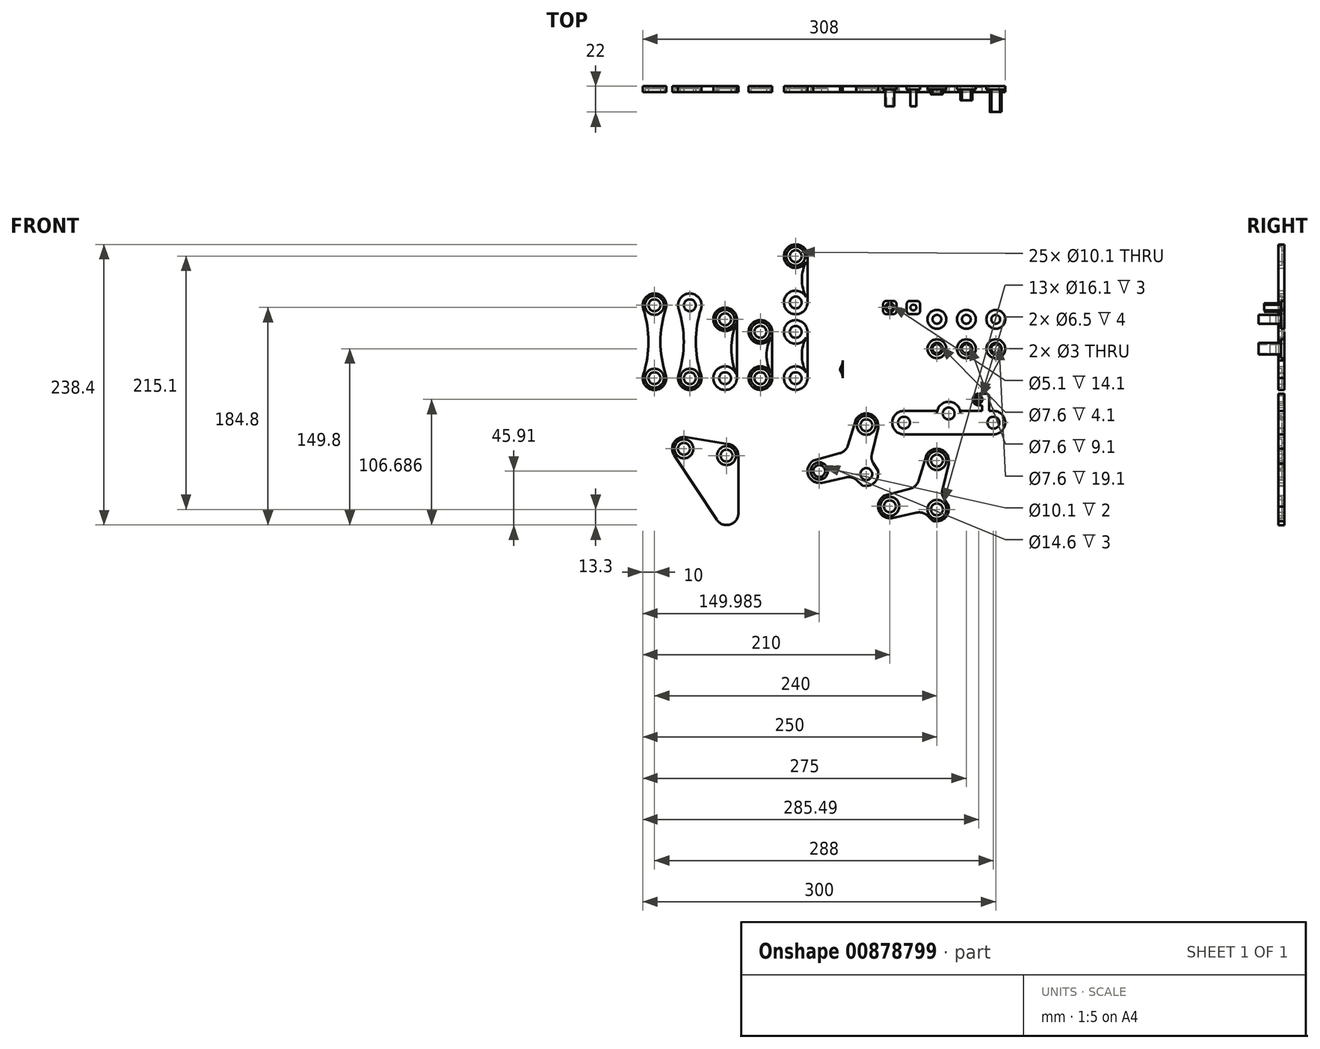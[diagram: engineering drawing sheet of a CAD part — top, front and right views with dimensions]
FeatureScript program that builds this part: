
annotation { "Feature Type Name" : "Feature", "Feature Type Description" : "" }
export const myFeature = defineFeature(function(context is Context, id is Id, definition is map)
    precondition{}
    {
        {
            assignVariable(context, id + "F0", {"name" : "thinkress", "anyValue" : 5});
        }
        {
            var Q0;
            Q0=qCreatedBy(makeId("Front.planeOp"),FACE);
            var sketch = newSketch(context, id + "F1", { "sketchPlane" : qUnion([Q0])});
            skArc(sketch, "E0", {"start": v(-10, 15) * mm, "mid": v(-20, 25) * mm, "end": v(-30, 15) * mm});
            skLineSegment(sketch, "E1", {"start": v(-30, 15) * mm, "end": v(-30, 0) * mm});
            skLineSegment(sketch, "E2", {"start": v(-10, 15) * mm, "end": v(-10, 0) * mm});
            skCircle(sketch, "E3", {"center": v(-20, 15) * mm, "radius": 5.05 * mm});
            skCircle(sketch, "E4", {"center": v(-20, 0) * mm, "radius": 5.05 * mm});
            skArc(sketch, "E5", {"start": v(-60, 0) * mm, "mid": v(-50, -10) * mm, "end": v(-40, 0) * mm});
            skArc(sketch, "E6", {"start": v(-40, 39.3) * mm, "mid": v(-50, 49.3) * mm, "end": v(-60, 39.3) * mm});
            skLineSegment(sketch, "E7", {"start": v(-60, 39.3) * mm, "end": v(-60, 0) * mm});
            skLineSegment(sketch, "E8", {"start": v(-40, 39.3) * mm, "end": v(-40, 0) * mm});
            skCircle(sketch, "E9", {"center": v(-50, 39.3) * mm, "radius": 5.05 * mm});
            skCircle(sketch, "E10", {"center": v(-50, 0) * mm, "radius": 5.05 * mm});
            skArc(sketch, "E11", {"start": v(-90, 0) * mm, "mid": v(-80, -10) * mm, "end": v(-70, 0) * mm});
            skArc(sketch, "E12", {"start": v(-70, 39.4) * mm, "mid": v(-80, 49.4) * mm, "end": v(-90, 39.4) * mm});
            skLineSegment(sketch, "E13", {"start": v(-90, 39.4) * mm, "end": v(-90, 0) * mm});
            skLineSegment(sketch, "E14", {"start": v(-70, 39.4) * mm, "end": v(-70, 0) * mm});
            skCircle(sketch, "E15", {"center": v(-80, 39.4) * mm, "radius": 5.05 * mm});
            skCircle(sketch, "E16", {"center": v(-80, 0) * mm, "radius": 5.05 * mm});
            skArc(sketch, "E17", {"start": v(-120, 0) * mm, "mid": v(-110, -10) * mm, "end": v(-100, 0) * mm});
            skArc(sketch, "E18", {"start": v(-100, 50) * mm, "mid": v(-110, 60) * mm, "end": v(-120, 50) * mm});
            skLineSegment(sketch, "E19", {"start": v(-120, 50) * mm, "end": v(-120, 0) * mm});
            skLineSegment(sketch, "E20", {"start": v(-100, 50) * mm, "end": v(-100, 0) * mm});
            skCircle(sketch, "E21", {"center": v(-110, 50) * mm, "radius": 5.05 * mm});
            skCircle(sketch, "E22", {"center": v(-110, 0) * mm, "radius": 5.05 * mm});
            skArc(sketch, "E23", {"start": v(-150, 0) * mm, "mid": v(-140, -10) * mm, "end": v(-130, 0) * mm});
            skArc(sketch, "E24", {"start": v(-130, 61.9) * mm, "mid": v(-140, 71.9) * mm, "end": v(-150, 61.9) * mm});
            skLineSegment(sketch, "E25", {"start": v(-150, 61.9) * mm, "end": v(-150, 0) * mm});
            skLineSegment(sketch, "E26", {"start": v(-130, 61.9) * mm, "end": v(-130, 0) * mm});
            skCircle(sketch, "E27", {"center": v(-140, 61.9) * mm, "radius": 5.05 * mm});
            skCircle(sketch, "E28", {"center": v(-140, 0) * mm, "radius": 5.05 * mm});
            skLineSegment(sketch, "E29", {"start": v(10, -81.5) * mm, "end": v(10, -40) * mm, "construction": true});
            skLineSegment(sketch, "E30", {"start": v(10, -40) * mm, "end": v(-30.01, -78.9) * mm, "construction": true});
            skLineSegment(sketch, "E31", {"start": v(-30.01, -78.9) * mm, "end": v(10, -81.5) * mm, "construction": true});
            skLineSegment(sketch, "E32", {"start": v(-145, -60) * mm, "end": v(-108.76, -65.8) * mm, "construction": true});
            skPoint(sketch, "E32.startSnap0", {"position": v(-80, -10) * mm});
            skLineSegment(sketch, "E33", {"start": v(-108.76, -65.8) * mm, "end": v(-108.76, -114.8) * mm, "construction": true});
            skLineSegment(sketch, "E34", {"start": v(-108.76, -114.8) * mm, "end": v(-145, -60) * mm, "construction": true});
            skArc(sketch, "E35", {"start": v(20, -40) * mm, "mid": v(13.9, -30.79) * mm, "end": v(3.03, -32.83) * mm});
            skArc(sketch, "E36", {"start": v(9.35, -91.48) * mm, "mid": v(16.84, -88.8) * mm, "end": v(20, -81.5) * mm});
            skArc(sketch, "E37", {"start": v(-36.98, -71.72) * mm, "mid": v(-39.4, -82.35) * mm, "end": v(-30.67, -88.87) * mm});
            skLineSegment(sketch, "E38.0", {"start": v(3.03, -32.83) * mm, "end": v(-36.98, -71.72) * mm});
            skLineSegment(sketch, "E39.0", {"start": v(20, -81.5) * mm, "end": v(20, -40) * mm});
            skLineSegment(sketch, "E40.0", {"start": v(-30.67, -88.87) * mm, "end": v(9.35, -91.48) * mm});
            skCircle(sketch, "E41", {"center": v(-30.01, -78.9) * mm, "radius": 5.05 * mm});
            skCircle(sketch, "E42", {"center": v(10, -40) * mm, "radius": 5.05 * mm});
            skCircle(sketch, "E43", {"center": v(10, -81.5) * mm, "radius": 5.05 * mm});
            skArc(sketch, "E44", {"start": v(-143.42, -50.13) * mm, "mid": v(-153.4, -54.58) * mm, "end": v(-153.34, -65.52) * mm});
            skArc(sketch, "E45", {"start": v(-117.1, -120.32) * mm, "mid": v(-105.88, -124.38) * mm, "end": v(-98.76, -114.8) * mm});
            skArc(sketch, "E46", {"start": v(-98.76, -65.8) * mm, "mid": v(-101.15, -59.31) * mm, "end": v(-107.18, -55.93) * mm});
            skLineSegment(sketch, "E47.0", {"start": v(-117.1, -120.32) * mm, "end": v(-153.34, -65.52) * mm});
            skLineSegment(sketch, "E48.0", {"start": v(-143.42, -50.13) * mm, "end": v(-107.18, -55.93) * mm});
            skLineSegment(sketch, "E49.0", {"start": v(-98.76, -65.8) * mm, "end": v(-98.76, -114.8) * mm});
            skCircle(sketch, "E50", {"center": v(-145, -60) * mm, "radius": 5.05 * mm});
            skCircle(sketch, "E51", {"center": v(-108.76, -65.8) * mm, "radius": 5.05 * mm});
            skLineSegment(sketch, "E52", {"start": v(42, -37.8) * mm, "end": v(80, -37.8) * mm, "construction": true});
            skLineSegment(sketch, "E53", {"start": v(80, -37.8) * mm, "end": v(118, -37.8) * mm, "construction": true});
            skLineSegment(sketch, "E54", {"start": v(80, -37.8) * mm, "end": v(80, -30) * mm, "construction": true});
            skArc(sketch, "E55", {"start": v(42, -27.8) * mm, "mid": v(32, -37.8) * mm, "end": v(42, -47.8) * mm});
            skArc(sketch, "E56", {"start": v(118, -47.8) * mm, "mid": v(128, -37.8) * mm, "end": v(118, -27.8) * mm});
            skArc(sketch, "E57", {"start": v(90, -30) * mm, "mid": v(80, -20) * mm, "end": v(70, -30) * mm});
            skLineSegment(sketch, "E58", {"start": v(42, -47.8) * mm, "end": v(118, -47.8) * mm});
            skLineSegment(sketch, "E59", {"start": v(42, -27.8) * mm, "end": v(70, -27.8) * mm});
            skLineSegment(sketch, "E60", {"start": v(70, -27.8) * mm, "end": v(70, -30) * mm});
            skLineSegment(sketch, "E61", {"start": v(118, -27.8) * mm, "end": v(114.5, -27.8) * mm});
            skLineSegment(sketch, "E62", {"start": v(90, -27.8) * mm, "end": v(90, -30) * mm});
            skCircle(sketch, "E63", {"center": v(80, -30) * mm, "radius": 5.05 * mm});
            skCircle(sketch, "E64", {"center": v(118, -37.8) * mm, "radius": 5.05 * mm});
            skCircle(sketch, "E65", {"center": v(42, -37.8) * mm, "radius": 5.05 * mm});
            skArc(sketch, "E66", {"start": v(-30, 0) * mm, "mid": v(-20, -10) * mm, "end": v(-10, 0) * mm});
            skArc(sketch, "E67", {"start": v(-180, 0) * mm, "mid": v(-170, -10) * mm, "end": v(-160, 0) * mm});
            skArc(sketch, "E68", {"start": v(-160, 61.9) * mm, "mid": v(-170, 71.9) * mm, "end": v(-180, 61.9) * mm});
            skLineSegment(sketch, "E69", {"start": v(-180, 61.9) * mm, "end": v(-180, 0) * mm});
            skLineSegment(sketch, "E70", {"start": v(-160, 61.9) * mm, "end": v(-160, 0) * mm});
            skCircle(sketch, "E71", {"center": v(-170, 61.9) * mm, "radius": 5.05 * mm});
            skCircle(sketch, "E72", {"center": v(-170, 0) * mm, "radius": 5.05 * mm});
            skLineSegment(sketch, "E73", {"start": v(70, -111.5) * mm, "end": v(70, -70) * mm, "construction": true});
            skLineSegment(sketch, "E74", {"start": v(70, -70) * mm, "end": v(29.99, -108.9) * mm, "construction": true});
            skLineSegment(sketch, "E75", {"start": v(29.99, -108.9) * mm, "end": v(70, -111.5) * mm, "construction": true});
            skArc(sketch, "E76", {"start": v(80, -70) * mm, "mid": v(73.9, -60.79) * mm, "end": v(63.03, -62.83) * mm});
            skArc(sketch, "E77", {"start": v(69.35, -121.48) * mm, "mid": v(76.84, -118.8) * mm, "end": v(80, -111.5) * mm});
            skArc(sketch, "E78", {"start": v(23.02, -101.72) * mm, "mid": v(20.6, -112.35) * mm, "end": v(29.33, -118.87) * mm});
            skLineSegment(sketch, "E79.0", {"start": v(63.03, -62.83) * mm, "end": v(23.02, -101.72) * mm});
            skLineSegment(sketch, "E80.0", {"start": v(80, -111.5) * mm, "end": v(80, -70) * mm});
            skLineSegment(sketch, "E81.0", {"start": v(29.33, -118.87) * mm, "end": v(69.35, -121.48) * mm});
            skCircle(sketch, "E82", {"center": v(29.99, -108.9) * mm, "radius": 5.05 * mm});
            skCircle(sketch, "E83", {"center": v(70, -70) * mm, "radius": 5.05 * mm});
            skCircle(sketch, "E84", {"center": v(70, -111.5) * mm, "radius": 5.05 * mm});
            skArc(sketch, "E85", {"start": v(-60, 64.3) * mm, "mid": v(-50, 54.3) * mm, "end": v(-40, 64.3) * mm});
            skArc(sketch, "E86", {"start": v(-40, 103.6) * mm, "mid": v(-50, 113.6) * mm, "end": v(-60, 103.6) * mm});
            skLineSegment(sketch, "E87", {"start": v(-60, 103.6) * mm, "end": v(-60, 64.3) * mm});
            skLineSegment(sketch, "E88", {"start": v(-40, 103.6) * mm, "end": v(-40, 64.3) * mm});
            skCircle(sketch, "E89", {"center": v(-50, 103.6) * mm, "radius": 5.05 * mm});
            skCircle(sketch, "E90", {"center": v(-50, 64.3) * mm, "radius": 5.05 * mm});
            skLineSegment(sketch, "E91", {"start": v(80, -18.11) * mm, "end": v(105.49, -18.11) * mm, "construction": true});
            skLineSegment(sketch, "E92", {"start": v(108.5, -27.8) * mm, "end": v(108.5, -24.11) * mm});
            skLineSegment(sketch, "E93", {"start": v(114.5, -27.8) * mm, "end": v(114.5, -15.61) * mm});
            skLineSegment(sketch, "E94.bottom", {"start": v(107.5, -23.11) * mm, "end": v(105.5, -23.11) * mm});
            skLineSegment(sketch, "E94.top", {"start": v(112, -13.11) * mm, "end": v(105.49, -13.11) * mm});
            skLineSegment(sketch, "E94.right", {"start": v(100.5, -18.11) * mm, "end": v(100.5, -18.11) * mm});
            skCircle(sketch, "E95", {"center": v(105.49, -18.11) * mm, "radius": 3.25 * mm});
            skLineSegment(sketch, "E96", {"start": v(80, -30) * mm, "end": v(80, -18.11) * mm, "construction": true});
            skPoint(sketch, "E97.visualSharp", {"position": v(100.5, -13.11) * mm});
            skArc(sketch, "E97.filletArc", {"start": v(105.49, -13.11) * mm, "mid": v(101.95, -14.58) * mm, "end": v(100.49, -18.11) * mm});
            skPoint(sketch, "E98.visualSharp", {"position": v(100.49, -23.11) * mm});
            skArc(sketch, "E98.filletArc", {"start": v(100.49, -18.11) * mm, "mid": v(101.95, -21.65) * mm, "end": v(105.5, -23.11) * mm});
            skPoint(sketch, "E99.visualSharp", {"position": v(114.5, -13.11) * mm});
            skArc(sketch, "E99.filletArc", {"start": v(114.5, -15.61) * mm, "mid": v(113.77, -13.85) * mm, "end": v(112, -13.11) * mm});
            skPoint(sketch, "E100.visualSharp", {"position": v(108.5, -23.11) * mm});
            skArc(sketch, "E100.filletArc", {"start": v(108.5, -24.11) * mm, "mid": v(108.2, -23.4) * mm, "end": v(107.5, -23.11) * mm});
            skLineSegment(sketch, "E101.trimOffspring", {"start": v(108.5, -27.8) * mm, "end": v(90, -27.8) * mm});
            skSolve(sketch);
        }
        {
            var Q0;
            Q0=makeQuery(id+"F1.imprint","IMPRINT",FACE,{"disambiguationData":[TD([[makeQuery(id+"F1.imprint","IMPRINT",EDGE,{"derivedFrom":sQuery(id+"F1.wireOp",EDGE,"E35")}),1.0]])]});
            var Q1;
            Q1=makeQuery(id+"F1.imprint","IMPRINT",FACE,{"disambiguationData":[TD([[makeQuery(id+"F1.imprint","IMPRINT",EDGE,{"derivedFrom":sQuery(id+"F1.wireOp",EDGE,"E44")}),1.0]])]});
            var Q2;
            Q2=makeQuery(id+"F1.imprint","IMPRINT",FACE,{"disambiguationData":[TD([[makeQuery(id+"F1.imprint","IMPRINT",EDGE,{"derivedFrom":sQuery(id+"F1.wireOp",EDGE,"E23")}),1.0]])]});
            var Q3;
            Q3=makeQuery(id+"F1.imprint","IMPRINT",FACE,{"disambiguationData":[TD([[makeQuery(id+"F1.imprint","IMPRINT",EDGE,{"derivedFrom":sQuery(id+"F1.wireOp",EDGE,"E17")}),1.0]])]});
            var Q4;
            Q4=makeQuery(id+"F1.imprint","IMPRINT",FACE,{"disambiguationData":[TD([[makeQuery(id+"F1.imprint","IMPRINT",EDGE,{"derivedFrom":sQuery(id+"F1.wireOp",EDGE,"E11")}),1.0]])]});
            var Q5;
            Q5=makeQuery(id+"F1.imprint","IMPRINT",FACE,{"disambiguationData":[TD([[makeQuery(id+"F1.imprint","IMPRINT",EDGE,{"derivedFrom":sQuery(id+"F1.wireOp",EDGE,"E5")}),1.0]])]});
            var Q6;
            Q6=makeQuery(id+"F1.imprint","IMPRINT",FACE,{"disambiguationData":[TD([[makeQuery(id+"F1.imprint","IMPRINT",EDGE,{"derivedFrom":sQuery(id+"F1.wireOp",EDGE,"EmJazmCR-fPvo-Zdi6-Hvz8-qesBlYHY8SAY")}),1.0]])]});
            var Q7;
            Q7=makeQuery(id+"F1.imprint","IMPRINT",FACE,{"disambiguationData":[TD([[makeQuery(id+"F1.imprint","IMPRINT",EDGE,{"derivedFrom":sQuery(id+"F1.wireOp",EDGE,"E55")}),1.0]])]});
            var Q8;
            Q8=makeQuery(id+"F1.imprint","IMPRINT",FACE,{"disambiguationData":[TD([[makeQuery(id+"F1.imprint","IMPRINT",EDGE,{"derivedFrom":sQuery(id+"F1.wireOp",EDGE,"E0")}),1.0]])]});
            var Q9;
            Q9=makeQuery(id+"F1.imprint","IMPRINT",FACE,{"disambiguationData":[TD([[makeQuery(id+"F1.imprint","IMPRINT",EDGE,{"derivedFrom":sQuery(id+"F1.wireOp",EDGE,"E67")}),1.0]])]});
            var Q10;
            Q10=makeQuery(id+"F1.imprint","IMPRINT",FACE,{"disambiguationData":[TD([[makeQuery(id+"F1.imprint","IMPRINT",EDGE,{"derivedFrom":sQuery(id+"F1.wireOp",EDGE,"E85")}),1.0]])]});
            var Q11;
            Q11=makeQuery(id+"F1.imprint","IMPRINT",FACE,{"disambiguationData":[TD([[makeQuery(id+"F1.imprint","IMPRINT",EDGE,{"derivedFrom":sQuery(id+"F1.wireOp",EDGE,"E76")}),1.0]])]});
            extrude(context, id + "F2", {"entities" : qUnion([Q0, Q1, Q2, Q3, Q4, Q5, Q6, Q7, Q8, Q9, Q10, Q11]), "depth" : (getVariable(context, 'thinkress')) * mm, "offsetDistance" : 25 * mm});
        }
        {
            var Q0;
            Q0=makeQuery(id+"F2.opExtrude","CAP_FACE",FACE,{"disambiguationData":[OSD([sQuery(id+"F1.wireOp",EDGE,"E23"),sQuery(id+"F1.wireOp",EDGE,"E24"),sQuery(id+"F1.wireOp",EDGE,"E25"),sQuery(id+"F1.wireOp",EDGE,"E26"),sQuery(id+"F1.wireOp",EDGE,"E27"),sQuery(id+"F1.wireOp",EDGE,"E28")])],"isStart":false});
            var sketch = newSketch(context, id + "F3", { "sketchPlane" : qUnion([Q0])});
            skArc(sketch, "E102", {"start": v(-130, 43.4) * mm, "mid": v(-135, 38.4) * mm, "end": v(-130, 33.4) * mm});
            skLineSegment(sketch, "E103.0", {"start": v(-130, 43.4) * mm, "end": v(-130, 33.4) * mm});
            skPoint(sketch, "E104.orphan", {"position": v(-130, 61.9) * mm});
            skPoint(sketch, "E105.orphan", {"position": v(-130, 0) * mm});
            skArc(sketch, "E106", {"start": v(-160, 43.4) * mm, "mid": v(-165, 38.4) * mm, "end": v(-160, 33.4) * mm});
            skLineSegment(sketch, "E107.0", {"start": v(-160, 43.4) * mm, "end": v(-160, 33.4) * mm});
            skPoint(sketch, "E108.orphan", {"position": v(-160, 61.9) * mm});
            skArc(sketch, "E109.0", {"start": v(-10, 15) * mm, "mid": v(-20, 25) * mm, "end": v(-30, 15) * mm});
            skArc(sketch, "E110.0", {"start": v(-30, 0) * mm, "mid": v(-20, -10) * mm, "end": v(-10, 0) * mm});
            skArc(sketch, "E111", {"start": v(-28.44, 5.36) * mm, "mid": v(-20, -10) * mm, "end": v(-11.56, 5.36) * mm});
            skArc(sketch, "E112", {"start": v(-11.56, 9.64) * mm, "mid": v(-20, 25) * mm, "end": v(-28.44, 9.64) * mm});
            skArc(sketch, "E113", {"start": v(-28.44, 5.36) * mm, "mid": v(-27.82, 7.5) * mm, "end": v(-28.44, 9.64) * mm});
            skLineSegment(sketch, "E114", {"start": v(-20, 15) * mm, "end": v(-20, 0) * mm, "construction": true});
            skArc(sketch, "E115.MirrorCS", {"start": v(-11.56, 5.36) * mm, "mid": v(-12.18, 7.5) * mm, "end": v(-11.56, 9.64) * mm});
            skLineSegment(sketch, "E116", {"start": v(-30, 15) * mm, "end": v(-30, 0) * mm});
            skLineSegment(sketch, "E117", {"start": v(-10, 15) * mm, "end": v(-10, 0) * mm});
            skArc(sketch, "E118.0", {"start": v(-40, 39.3) * mm, "mid": v(-50, 49.3) * mm, "end": v(-60, 39.3) * mm});
            skArc(sketch, "E119.0", {"start": v(-60, 0) * mm, "mid": v(-50, -10) * mm, "end": v(-40, 0) * mm});
            skCircle(sketch, "E120", {"center": v(-50, 39.3) * mm, "radius": 10 * mm});
            skCircle(sketch, "E121", {"center": v(-50, 0) * mm, "radius": 10 * mm});
            skArc(sketch, "E122", {"start": v(-58.9, 4.57) * mm, "mid": v(-55.25, 19.65) * mm, "end": v(-58.9, 34.73) * mm});
            skLineSegment(sketch, "E123", {"start": v(-50, 39.3) * mm, "end": v(-50, 0) * mm, "construction": true});
            skArc(sketch, "E124.MirrorCS", {"start": v(-41.1, 4.57) * mm, "mid": v(-44.75, 19.65) * mm, "end": v(-41.1, 34.73) * mm});
            skLineSegment(sketch, "E125", {"start": v(-60, 39.3) * mm, "end": v(-60, 0) * mm});
            skLineSegment(sketch, "E126", {"start": v(-40, 39.3) * mm, "end": v(-40, 0) * mm});
            skArc(sketch, "E127.0", {"start": v(-70, 39.4) * mm, "mid": v(-80, 49.4) * mm, "end": v(-90, 39.4) * mm});
            skArc(sketch, "E128.0", {"start": v(-90, 0) * mm, "mid": v(-80, -10) * mm, "end": v(-70, 0) * mm});
            skCircle(sketch, "E129", {"center": v(-80, 39.4) * mm, "radius": 10 * mm});
            skCircle(sketch, "E130", {"center": v(-80, 0) * mm, "radius": 10 * mm});
            skArc(sketch, "E131", {"start": v(-88.89, 4.58) * mm, "mid": v(-85.22, 19.7) * mm, "end": v(-88.89, 34.82) * mm});
            skLineSegment(sketch, "E132", {"start": v(-80, 38.26) * mm, "end": v(-80, 0) * mm, "construction": true});
            skLineSegment(sketch, "E133", {"start": v(-90, 39.4) * mm, "end": v(-90, 0) * mm});
            skArc(sketch, "E134.MirrorCS", {"start": v(-71.11, 4.58) * mm, "mid": v(-74.78, 19.7) * mm, "end": v(-71.11, 34.82) * mm});
            skLineSegment(sketch, "E135.MirrorCS", {"start": v(-70, 39.4) * mm, "end": v(-70, 0) * mm});
            skArc(sketch, "E136.0", {"start": v(-40, 103.6) * mm, "mid": v(-50, 113.6) * mm, "end": v(-60, 103.6) * mm});
            skArc(sketch, "E137.0", {"start": v(-60, 64.3) * mm, "mid": v(-50, 54.3) * mm, "end": v(-40, 64.3) * mm});
            skCircle(sketch, "E138", {"center": v(-50, 103.6) * mm, "radius": 10 * mm});
            skCircle(sketch, "E139", {"center": v(-50, 64.3) * mm, "radius": 10 * mm});
            skArc(sketch, "E140", {"start": v(-58.9, 68.87) * mm, "mid": v(-55.25, 83.95) * mm, "end": v(-58.9, 99.03) * mm});
            skLineSegment(sketch, "E141", {"start": v(-50, 103.6) * mm, "end": v(-50, 64.3) * mm, "construction": true});
            skLineSegment(sketch, "E142", {"start": v(-60, 103.6) * mm, "end": v(-60, 64.3) * mm});
            skArc(sketch, "E143.MirrorCS", {"start": v(-41.1, 68.87) * mm, "mid": v(-44.75, 83.95) * mm, "end": v(-41.1, 99.03) * mm});
            skLineSegment(sketch, "E144.MirrorCS", {"start": v(-40, 103.6) * mm, "end": v(-40, 64.3) * mm});
            skArc(sketch, "E145.0", {"start": v(-100, 50) * mm, "mid": v(-110, 60) * mm, "end": v(-120, 50) * mm});
            skArc(sketch, "E146.0", {"start": v(-120, 0) * mm, "mid": v(-110, -10) * mm, "end": v(-100, 0) * mm});
            skCircle(sketch, "E147", {"center": v(-110, 0) * mm, "radius": 10 * mm});
            skCircle(sketch, "E148", {"center": v(-110, 50) * mm, "radius": 10 * mm});
            skArc(sketch, "E149", {"start": v(-119.34, 3.57) * mm, "mid": v(-115.38, 25) * mm, "end": v(-119.34, 46.43) * mm});
            skLineSegment(sketch, "E150", {"start": v(-110, 50) * mm, "end": v(-110, 0) * mm, "construction": true});
            skLineSegment(sketch, "E151", {"start": v(-120, 50) * mm, "end": v(-120, 0) * mm});
            skArc(sketch, "E152.MirrorCS", {"start": v(-100.66, 3.57) * mm, "mid": v(-104.62, 25) * mm, "end": v(-100.66, 46.43) * mm});
            skLineSegment(sketch, "E153.MirrorCS", {"start": v(-100, 50) * mm, "end": v(-100, 0) * mm});
            skPoint(sketch, "E154.0", {"position": v(-140, 71.9) * mm});
            skArc(sketch, "E155.0", {"start": v(-150, 0) * mm, "mid": v(-140, -10) * mm, "end": v(-130, 0) * mm});
            skArc(sketch, "E156.0", {"start": v(-130, 61.9) * mm, "mid": v(-140, 71.9) * mm, "end": v(-150, 61.9) * mm});
            skCircle(sketch, "E157", {"center": v(-140, 61.9) * mm, "radius": 10 * mm});
            skCircle(sketch, "E158", {"center": v(-140, 0) * mm, "radius": 10 * mm});
            skArc(sketch, "E159", {"start": v(-149.5, 3.1) * mm, "mid": v(-145.09, 30.95) * mm, "end": v(-149.5, 58.8) * mm});
            skLineSegment(sketch, "E160", {"start": v(-140, 61.9) * mm, "end": v(-140, 0) * mm, "construction": true});
            skLineSegment(sketch, "E161", {"start": v(-150, 61.9) * mm, "end": v(-150, 0) * mm});
            skArc(sketch, "E162.MirrorCS", {"start": v(-130.5, 3.1) * mm, "mid": v(-134.91, 30.95) * mm, "end": v(-130.5, 58.8) * mm});
            skLineSegment(sketch, "E163.MirrorCS", {"start": v(-130, 61.9) * mm, "end": v(-130, 0) * mm});
            skArc(sketch, "E164.0", {"start": v(-160, 61.9) * mm, "mid": v(-170, 71.9) * mm, "end": v(-180, 61.9) * mm});
            skArc(sketch, "E165.0", {"start": v(-180, 0) * mm, "mid": v(-170, -10) * mm, "end": v(-160, 0) * mm});
            skCircle(sketch, "E166", {"center": v(-170, 0) * mm, "radius": 10 * mm});
            skCircle(sketch, "E167", {"center": v(-170, 61.9) * mm, "radius": 10 * mm});
            skArc(sketch, "E168", {"start": v(-179.5, 3.1) * mm, "mid": v(-175.09, 30.95) * mm, "end": v(-179.5, 58.8) * mm});
            skLineSegment(sketch, "E169", {"start": v(-170, 61.9) * mm, "end": v(-170, 0) * mm, "construction": true});
            skLineSegment(sketch, "E170", {"start": v(-180, 61.9) * mm, "end": v(-180, 0) * mm});
            skArc(sketch, "E171.MirrorCS", {"start": v(-160.5, 3.1) * mm, "mid": v(-164.91, 30.95) * mm, "end": v(-160.5, 58.8) * mm});
            skLineSegment(sketch, "E172.MirrorCS", {"start": v(-160, 61.9) * mm, "end": v(-160, 0) * mm});
            skSolve(sketch);
        }
        {
            var Q0;
            Q0=makeQuery(id+"F3.imprint","IMPRINT",FACE,{"disambiguationData":[TD([[makeQuery(id+"F3.imprint","IMPRINT",EDGE,{"derivedFrom":sQuery(id+"F3.wireOp",EDGE,"E102")}),1.0]])]});
            var Q1;
            Q1=makeQuery(id+"F3.imprint","IMPRINT",FACE,{"disambiguationData":[TD([[makeQuery(id+"F3.imprint","IMPRINT",EDGE,{"derivedFrom":sQuery(id+"F3.wireOp",EDGE,"E106")}),1.0]])]});
            var Q2;
            {var subQ0=sQuery(id+"F3.wireOp",EDGE,"E113");Q2=makeQuery(id+"F3.imprint","IMPRINT",FACE,{"disambiguationData":[TD([[makeQuery(id+"F3.imprint","IMPRINT",EDGE,{"derivedFrom":subQ0}),1.0]])]});}
            var Q3;
            {var subQ0=sQuery(id+"F3.wireOp",EDGE,"E115.MirrorCS");Q3=makeQuery(id+"F3.imprint","IMPRINT",FACE,{"disambiguationData":[TD([[makeQuery(id+"F3.imprint","IMPRINT",EDGE,{"derivedFrom":subQ0}),-1.0]])]});}
            var Q4;
            {var subQ0=sQuery(id+"F3.wireOp",EDGE,"E122");Q4=makeQuery(id+"F3.imprint","IMPRINT",FACE,{"disambiguationData":[TD([[makeQuery(id+"F3.imprint","IMPRINT",EDGE,{"derivedFrom":subQ0}),1.0]])]});}
            var Q5;
            {var subQ0=sQuery(id+"F3.wireOp",EDGE,"E124.MirrorCS");Q5=makeQuery(id+"F3.imprint","IMPRINT",FACE,{"disambiguationData":[TD([[makeQuery(id+"F3.imprint","IMPRINT",EDGE,{"derivedFrom":subQ0}),-1.0]])]});}
            var Q6;
            {var subQ0=sQuery(id+"F3.wireOp",EDGE,"E131");Q6=makeQuery(id+"F3.imprint","IMPRINT",FACE,{"disambiguationData":[TD([[makeQuery(id+"F3.imprint","IMPRINT",EDGE,{"derivedFrom":subQ0}),1.0]])]});}
            var Q7;
            {var subQ0=sQuery(id+"F3.wireOp",EDGE,"E134.MirrorCS");Q7=makeQuery(id+"F3.imprint","IMPRINT",FACE,{"disambiguationData":[TD([[makeQuery(id+"F3.imprint","IMPRINT",EDGE,{"derivedFrom":subQ0}),-1.0]])]});}
            var Q8;
            {var subQ0=sQuery(id+"F3.wireOp",EDGE,"E152.MirrorCS");Q8=makeQuery(id+"F3.imprint","IMPRINT",FACE,{"disambiguationData":[TD([[makeQuery(id+"F3.imprint","IMPRINT",EDGE,{"derivedFrom":subQ0}),-1.0]])]});}
            var Q9;
            {var subQ0=sQuery(id+"F3.wireOp",EDGE,"E149");Q9=makeQuery(id+"F3.imprint","IMPRINT",FACE,{"disambiguationData":[TD([[makeQuery(id+"F3.imprint","IMPRINT",EDGE,{"derivedFrom":subQ0}),1.0]])]});}
            var Q10;
            {var subQ0=sQuery(id+"F3.wireOp",EDGE,"E140");Q10=makeQuery(id+"F3.imprint","IMPRINT",FACE,{"disambiguationData":[TD([[makeQuery(id+"F3.imprint","IMPRINT",EDGE,{"derivedFrom":subQ0}),1.0]])]});}
            var Q11;
            {var subQ0=sQuery(id+"F3.wireOp",EDGE,"E143.MirrorCS");Q11=makeQuery(id+"F3.imprint","IMPRINT",FACE,{"disambiguationData":[TD([[makeQuery(id+"F3.imprint","IMPRINT",EDGE,{"derivedFrom":subQ0}),-1.0]])]});}
            var Q12;
            {var subQ0=sQuery(id+"F3.wireOp",EDGE,"E163.MirrorCS");var subQ1=sQuery(id+"F3.wireOp",EDGE,"E102");var subQ2=makeQuery(id+"F3.imprint","INTERSECT",VERTEX,{"disambiguationData":[OD(1.0)],"derivedFrom":[subQ1,subQ0]});Q12=makeQuery(id+"F3.imprint","IMPRINT",FACE,{"disambiguationData":[TD([[makeQuery(id+"F3.imprint","IMPRINT",EDGE,{"disambiguationData":[TD([[subQ2,1.0]])],"derivedFrom":subQ1}),-1.0]])]});}
            var Q13;
            {var subQ0=sQuery(id+"F3.wireOp",EDGE,"E163.MirrorCS");var subQ1=sQuery(id+"F3.wireOp",EDGE,"E102");var subQ2=makeQuery(id+"F3.imprint","INTERSECT",VERTEX,{"disambiguationData":[OD(0.0)],"derivedFrom":[subQ1,subQ0]});Q13=makeQuery(id+"F3.imprint","IMPRINT",FACE,{"disambiguationData":[TD([[makeQuery(id+"F3.imprint","IMPRINT",EDGE,{"disambiguationData":[TD([[subQ2,-1.0]])],"derivedFrom":subQ1}),-1.0]])]});}
            var Q14;
            {var subQ0=sQuery(id+"F3.wireOp",EDGE,"E163.MirrorCS");var subQ1=sQuery(id+"F3.wireOp",EDGE,"E102");var subQ2=makeQuery(id+"F3.imprint","INTERSECT",VERTEX,{"disambiguationData":[OD(0.0)],"derivedFrom":[subQ1,subQ0]});Q14=makeQuery(id+"F3.imprint","IMPRINT",FACE,{"disambiguationData":[TD([[makeQuery(id+"F3.imprint","IMPRINT",EDGE,{"disambiguationData":[TD([[subQ2,-1.0]])],"derivedFrom":subQ1}),1.0]])]});}
            var Q15;
            {var subQ2=sQuery(id+"F3.wireOp",EDGE,"E159");Q15=makeQuery(id+"F3.imprint","IMPRINT",FACE,{"disambiguationData":[TD([[makeQuery(id+"F3.imprint","IMPRINT",EDGE,{"derivedFrom":subQ2}),1.0]])]});}
            var Q16;
            {var subQ0=sQuery(id+"F3.wireOp",EDGE,"E172.MirrorCS");var subQ1=sQuery(id+"F3.wireOp",EDGE,"E106");var subQ2=makeQuery(id+"F3.imprint","INTERSECT",VERTEX,{"disambiguationData":[OD(1.0)],"derivedFrom":[subQ1,subQ0]});Q16=makeQuery(id+"F3.imprint","IMPRINT",FACE,{"disambiguationData":[TD([[makeQuery(id+"F3.imprint","IMPRINT",EDGE,{"disambiguationData":[TD([[subQ2,1.0]])],"derivedFrom":subQ1}),-1.0]])]});}
            var Q17;
            {var subQ0=sQuery(id+"F3.wireOp",EDGE,"E172.MirrorCS");var subQ1=sQuery(id+"F3.wireOp",EDGE,"E106");var subQ2=makeQuery(id+"F3.imprint","INTERSECT",VERTEX,{"disambiguationData":[OD(0.0)],"derivedFrom":[subQ1,subQ0]});Q17=makeQuery(id+"F3.imprint","IMPRINT",FACE,{"disambiguationData":[TD([[makeQuery(id+"F3.imprint","IMPRINT",EDGE,{"disambiguationData":[TD([[subQ2,-1.0]])],"derivedFrom":subQ1}),1.0]])]});}
            var Q18;
            {var subQ0=sQuery(id+"F3.wireOp",EDGE,"E172.MirrorCS");var subQ1=sQuery(id+"F3.wireOp",EDGE,"E106");var subQ2=makeQuery(id+"F3.imprint","INTERSECT",VERTEX,{"disambiguationData":[OD(0.0)],"derivedFrom":[subQ1,subQ0]});Q18=makeQuery(id+"F3.imprint","IMPRINT",FACE,{"disambiguationData":[TD([[makeQuery(id+"F3.imprint","IMPRINT",EDGE,{"disambiguationData":[TD([[subQ2,-1.0]])],"derivedFrom":subQ1}),-1.0]])]});}
            var Q19;
            {var subQ0=sQuery(id+"F3.wireOp",EDGE,"E168");Q19=makeQuery(id+"F3.imprint","IMPRINT",FACE,{"disambiguationData":[TD([[makeQuery(id+"F3.imprint","IMPRINT",EDGE,{"derivedFrom":subQ0}),1.0]])]});}
            extrude(context, id + "F4", {"entities" : qUnion([Q0, Q1, Q2, Q3, Q4, Q5, Q6, Q7, Q8, Q9, Q10, Q11, Q12, Q13, Q14, Q15, Q16, Q17, Q18, Q19]), "operationType" : NewBodyOperationType.REMOVE, "endBound" : BoundingType.UP_TO_NEXT, "oppositeDirection" : true, "depth" : 25 * mm, "offsetDistance" : 25 * mm});
        }
        {
            assignVariable(context, id + "F5", {"name" : "nailRoundHigh", "anyValue" : 3});
        }
        {
            var Q0;
            Q0=makeQuery(id+"F2.opExtrude","CAP_FACE",FACE,{"disambiguationData":[OSD([sQuery(id+"F1.wireOp",EDGE,"E0"),sQuery(id+"F1.wireOp",EDGE,"E1"),sQuery(id+"F1.wireOp",EDGE,"E2"),sQuery(id+"F1.wireOp",EDGE,"E3"),sQuery(id+"F1.wireOp",EDGE,"E4"),sQuery(id+"F1.wireOp",EDGE,"E66")])],"isStart":false});
            var sketch = newSketch(context, id + "F6", { "sketchPlane" : qUnion([Q0])});
            skCircle(sketch, "E173", {"center": v(-20, 15) * mm, "radius": 8.05 * mm});
            skCircle(sketch, "E174", {"center": v(-80, 39.4) * mm, "radius": 8.05 * mm});
            skCircle(sketch, "E175", {"center": v(-140, 0) * mm, "radius": 8.05 * mm});
            skCircle(sketch, "E176", {"center": v(-170, 0) * mm, "radius": 8.05 * mm});
            skCircle(sketch, "E177", {"center": v(10, -40) * mm, "radius": 8.05 * mm});
            skCircle(sketch, "E178", {"center": v(-30.01, -78.9) * mm, "radius": 7.3 * mm});
            skCircle(sketch, "E179", {"center": v(-170, 61.9) * mm, "radius": 8.05 * mm});
            skCircle(sketch, "E180", {"center": v(70, -70) * mm, "radius": 8.05 * mm});
            skCircle(sketch, "E181", {"center": v(29.99, -108.9) * mm, "radius": 8.05 * mm});
            skCircle(sketch, "E182", {"center": v(-80, 0) * mm, "radius": 8.05 * mm});
            skCircle(sketch, "E183", {"center": v(-110, 50) * mm, "radius": 8.05 * mm});
            skCircle(sketch, "E184", {"center": v(-50, 103.6) * mm, "radius": 8.05 * mm});
            skCircle(sketch, "E185", {"center": v(70, -111.5) * mm, "radius": 8.05 * mm});
            skSolve(sketch);
        }
        {
            var Q0;
            Q0=qSketchRegion(id+"F6",true);
            extrude(context, id + "F7", {"entities" : qUnion([Q0]), "operationType" : NewBodyOperationType.REMOVE, "oppositeDirection" : true, "depth" : (getVariable(context, 'nailRoundHigh')) * mm, "offsetDistance" : 25 * mm});
        }
        {
            var Q0;
            Q0=makeQuery(id+"F2.opExtrude","CAP_FACE",FACE,{"disambiguationData":[OSD([sQuery(id+"F1.wireOp",EDGE,"E0"),sQuery(id+"F1.wireOp",EDGE,"E1"),sQuery(id+"F1.wireOp",EDGE,"E2"),sQuery(id+"F1.wireOp",EDGE,"E3"),sQuery(id+"F1.wireOp",EDGE,"E4"),sQuery(id+"F1.wireOp",EDGE,"E66")])],"isStart":true});
            var sketch = newSketch(context, id + "F8", { "sketchPlane" : qUnion([Q0])});
            skCircle(sketch, "E186", {"center": v(20, 0) * mm, "radius": 8.05 * mm});
            skLineSegment(sketch, "E187.bottom", {"start": v(25.7, 5.7) * mm, "end": v(14.3, 5.7) * mm});
            skLineSegment(sketch, "E187.top", {"start": v(25.7, -5.7) * mm, "end": v(14.3, -5.7) * mm});
            skLineSegment(sketch, "E187.left", {"start": v(25.7, 5.7) * mm, "end": v(25.7, -5.7) * mm});
            skLineSegment(sketch, "E187.right", {"start": v(14.3, 5.7) * mm, "end": v(14.3, -5.7) * mm});
            skSolve(sketch);
        }
        {
            var Q0;
            Q0=makeQuery(id+"F8.imprint","IMPRINT",FACE,{"disambiguationData":[TD([[makeQuery(id+"F8.imprint","IMPRINT",EDGE,{"derivedFrom":sQuery(id+"F8.wireOp",EDGE,"E187.bottom")}),1.0]])]});
            extrude(context, id + "F9", {"entities" : qUnion([Q0]), "operationType" : NewBodyOperationType.REMOVE, "oppositeDirection" : true, "depth" : (getVariable(context, 'nailRoundHigh')) * mm, "offsetDistance" : 25 * mm});
        }
        {
            var Q0;
            Q0=makeQuery(id+"F2.opExtrude","CAP_FACE",FACE,{"disambiguationData":[OSD([sQuery(id+"F1.wireOp",EDGE,"E44"),sQuery(id+"F1.wireOp",EDGE,"E45"),sQuery(id+"F1.wireOp",EDGE,"E46"),sQuery(id+"F1.wireOp",EDGE,"E47.0"),sQuery(id+"F1.wireOp",EDGE,"E48.0"),sQuery(id+"F1.wireOp",EDGE,"E49.0"),sQuery(id+"F1.wireOp",EDGE,"E50"),sQuery(id+"F1.wireOp",EDGE,"E51"),sQuery(id+"F1.wireOp",EDGE,"0d3phSLj-5KfE-gnTl-3xaD-v1bR61xUgd2v")])],"isStart":false});
            var sketch = newSketch(context, id + "F10", { "sketchPlane" : qUnion([Q0])});
            skCircle(sketch, "E188", {"center": v(-108.76, -65.8) * mm, "radius": 8.05 * mm});
            skCircle(sketch, "E189", {"center": v(-145, -60) * mm, "radius": 8.05 * mm});
            skSolve(sketch);
        }
        {
            var Q0;
            Q0=qSketchRegion(id+"F10",true);
            extrude(context, id + "F11", {"entities" : qUnion([Q0]), "operationType" : NewBodyOperationType.REMOVE, "oppositeDirection" : true, "depth" : (getVariable(context, 'nailRoundHigh')) * mm, "offsetDistance" : 25 * mm});
        }
        {
            var Q0;
            Q0=qCreatedBy(makeId("Front.planeOp"),FACE);
            var sketch = newSketch(context, id + "F12", { "sketchPlane" : qUnion([Q0])});
            skCircle(sketch, "E190", {"center": v(30, 60) * mm, "radius": 7.95 * mm});
            skLineSegment(sketch, "E191.bottom", {"start": v(35.62, 65.62) * mm, "end": v(24.38, 65.62) * mm});
            skLineSegment(sketch, "E191.top", {"start": v(35.62, 54.38) * mm, "end": v(24.38, 54.38) * mm});
            skLineSegment(sketch, "E191.left", {"start": v(35.62, 65.62) * mm, "end": v(35.62, 54.38) * mm});
            skLineSegment(sketch, "E191.right", {"start": v(24.38, 65.62) * mm, "end": v(24.38, 54.38) * mm});
            skCircle(sketch, "E192", {"center": v(50, 60) * mm, "radius": 7.95 * mm});
            skLineSegment(sketch, "E193.bottom", {"start": v(55.62, 65.62) * mm, "end": v(44.38, 65.62) * mm});
            skLineSegment(sketch, "E193.top", {"start": v(55.62, 54.38) * mm, "end": v(44.38, 54.38) * mm});
            skLineSegment(sketch, "E193.left", {"start": v(55.62, 65.62) * mm, "end": v(55.62, 54.38) * mm});
            skLineSegment(sketch, "E193.right", {"start": v(44.38, 65.62) * mm, "end": v(44.38, 54.38) * mm});
            skSolve(sketch);
        }
        {
            var Q0;
            Q0=qCreatedBy(makeId("Front.planeOp"),FACE);
            var sketch = newSketch(context, id + "F13", { "sketchPlane" : qUnion([Q0])});
            skCircle(sketch, "E194", {"center": v(70, 25) * mm, "radius": 8 * mm});
            skCircle(sketch, "E195", {"center": v(95, 25) * mm, "radius": 8 * mm});
            skCircle(sketch, "E196", {"center": v(120, 25) * mm, "radius": 8 * mm});
            skCircle(sketch, "E197", {"center": v(70, 50) * mm, "radius": 8 * mm});
            skCircle(sketch, "E198", {"center": v(95, 50) * mm, "radius": 8 * mm});
            skCircle(sketch, "E199", {"center": v(120, 50) * mm, "radius": 8 * mm});
            skSolve(sketch);
        }
        {
            var Q0;
            Q0=makeQuery(id+"F13.imprint","IMPRINT",FACE,{"disambiguationData":[TD([[makeQuery(id+"F13.imprint","IMPRINT",EDGE,{"derivedFrom":sQuery(id+"F13.wireOp",EDGE,"0Woy9mCR-aocV-ndQ5-0IHn-ZHNOPLBgyWjz")}),1.0]])]});
            var Q1;
            Q1=makeQuery(id+"F13.imprint","IMPRINT",FACE,{"disambiguationData":[TD([[makeQuery(id+"F13.imprint","IMPRINT",EDGE,{"derivedFrom":sQuery(id+"F13.wireOp",EDGE,"E194")}),1.0]])]});
            var Q2;
            Q2=makeQuery(id+"F13.imprint","IMPRINT",FACE,{"disambiguationData":[TD([[makeQuery(id+"F13.imprint","IMPRINT",EDGE,{"derivedFrom":sQuery(id+"F13.wireOp",EDGE,"E195")}),1.0]])]});
            var Q3;
            Q3=makeQuery(id+"F13.imprint","IMPRINT",FACE,{"disambiguationData":[TD([[makeQuery(id+"F13.imprint","IMPRINT",EDGE,{"derivedFrom":sQuery(id+"F13.wireOp",EDGE,"E196")}),1.0]])]});
            var Q4;
            Q4=makeQuery(id+"F13.imprint","IMPRINT",FACE,{"disambiguationData":[TD([[makeQuery(id+"F13.imprint","IMPRINT",EDGE,{"derivedFrom":sQuery(id+"F13.wireOp",EDGE,"96c4269c-3a78-4078-af1c-18907ede8449")}),1.0]])]});
            var Q5;
            Q5=makeQuery(id+"F13.imprint","IMPRINT",FACE,{"disambiguationData":[TD([[makeQuery(id+"F13.imprint","IMPRINT",EDGE,{"derivedFrom":sQuery(id+"F13.wireOp",EDGE,"E197")}),1.0]])]});
            var Q6;
            Q6=makeQuery(id+"F13.imprint","IMPRINT",FACE,{"disambiguationData":[TD([[makeQuery(id+"F13.imprint","IMPRINT",EDGE,{"derivedFrom":sQuery(id+"F13.wireOp",EDGE,"E198")}),1.0]])]});
            var Q7;
            Q7=makeQuery(id+"F13.imprint","IMPRINT",FACE,{"disambiguationData":[TD([[makeQuery(id+"F13.imprint","IMPRINT",EDGE,{"derivedFrom":sQuery(id+"F13.wireOp",EDGE,"E199")}),1.0]])]});
            var Q8;
            Q8=makeQuery(id+"F13.imprint","IMPRINT",FACE,{"disambiguationData":[TD([[makeQuery(id+"F13.imprint","IMPRINT",EDGE,{"derivedFrom":sQuery(id+"F13.wireOp",EDGE,"47c22200-7e39-4161-b108-0bee486872d6")}),1.0]])]});
            var Q9;
            Q9=makeQuery(id+"F12.imprint","IMPRINT",FACE,{"disambiguationData":[TD([[makeQuery(id+"F12.imprint","IMPRINT",EDGE,{"derivedFrom":sQuery(id+"F12.wireOp",EDGE,"E191.bottom")}),1.0]])]});
            var Q10;
            Q10=makeQuery(id+"F12.imprint","IMPRINT",FACE,{"disambiguationData":[TD([[makeQuery(id+"F12.imprint","IMPRINT",EDGE,{"derivedFrom":sQuery(id+"F12.wireOp",EDGE,"E193.bottom")}),1.0]])]});
            extrude(context, id + "F14", {"entities" : qUnion([Q0, Q1, Q2, Q3, Q4, Q5, Q6, Q7, Q8, Q9, Q10]), "depth" : (getVariable(context, 'nailRoundHigh') - 0.1) * mm, "offsetDistance" : 25 * mm});
        }
        {
            var Q0;
            Q0=makeQuery(id+"F14.opExtrude","CAP_FACE",FACE,{"disambiguationData":[OSD([sQuery(id+"F13.wireOp",EDGE,"E194")])],"isStart":false});
            var sketch = newSketch(context, id + "F15", { "sketchPlane" : qUnion([Q0])});
            skCircle(sketch, "E200", {"center": v(70, 25) * mm, "radius": 5 * mm});
            skCircle(sketch, "E201", {"center": v(95, 25) * mm, "radius": 5 * mm});
            skCircle(sketch, "E202", {"center": v(120, 25) * mm, "radius": 5 * mm});
            skCircle(sketch, "E203", {"center": v(70, 50) * mm, "radius": 3.75 * mm});
            skCircle(sketch, "E204", {"center": v(95, 50) * mm, "radius": 3.75 * mm});
            skCircle(sketch, "E205", {"center": v(120, 50) * mm, "radius": 3.75 * mm});
            skCircle(sketch, "E206", {"center": v(70, 25) * mm, "radius": 3.8 * mm});
            skCircle(sketch, "E207", {"center": v(95, 25) * mm, "radius": 3.8 * mm});
            skCircle(sketch, "E208", {"center": v(120, 25) * mm, "radius": 3.8 * mm});
            skLineSegment(sketch, "E209.0", {"start": v(35.62, 65.62) * mm, "end": v(24.38, 65.62) * mm, "construction": true});
            skLineSegment(sketch, "E210.0", {"start": v(35.62, 65.62) * mm, "end": v(35.62, 54.38) * mm, "construction": true});
            skLineSegment(sketch, "E211", {"start": v(30, 65.62) * mm, "end": v(30, 56.2) * mm, "construction": true});
            skLineSegment(sketch, "E212", {"start": v(35.62, 60) * mm, "end": v(24.91, 60) * mm, "construction": true});
            skCircle(sketch, "E213", {"center": v(50, 60) * mm, "radius": 2.5 * mm});
            skLineSegment(sketch, "E214.0", {"start": v(55.62, 65.62) * mm, "end": v(44.38, 65.62) * mm});
            skLineSegment(sketch, "E215.0", {"start": v(44.38, 65.62) * mm, "end": v(44.38, 54.38) * mm});
            skLineSegment(sketch, "E216", {"start": v(50, 65.54) * mm, "end": v(50, 54.74) * mm, "construction": true});
            skPoint(sketch, "E216.startSnap0", {"position": v(50, 65.62) * mm});
            skLineSegment(sketch, "E217", {"start": v(45.24, 60) * mm, "end": v(54.76, 60) * mm, "construction": true});
            skPoint(sketch, "E217.startSnap0", {"position": v(44.38, 60) * mm});
            skCircle(sketch, "E218", {"center": v(30, 60) * mm, "radius": 3.75 * mm});
            skCircle(sketch, "E219", {"center": v(30, 60) * mm, "radius": 2.55 * mm});
            skSolve(sketch);
        }
        {
            assignVariable(context, id + "F16", {"name" : "mistakeLength", "anyValue" : 0.1});
        }
        {
            var Q0;
            Q0=makeQuery(id+"F15.imprint","IMPRINT",FACE,{"disambiguationData":[TD([[makeQuery(id+"F15.imprint","IMPRINT",EDGE,{"derivedFrom":sQuery(id+"F15.wireOp",EDGE,"E200")}),1.0]])]});
            var Q1;
            Q1=makeQuery(id+"F15.imprint","IMPRINT",FACE,{"disambiguationData":[TD([[makeQuery(id+"F15.imprint","IMPRINT",EDGE,{"derivedFrom":sQuery(id+"F15.wireOp",EDGE,"E203")}),1.0]])]});
            extrude(context, id + "F17", {"entities" : qUnion([Q0, Q1]), "operationType" : NewBodyOperationType.ADD, "depth" : (getVariable(context, 'mistakeLength') + getVariable(context, 'thinkress') * 2 - getVariable(context, 'nailRoundHigh') * 2) * mm, "offsetDistance" : 25 * mm});
        }
        {
            var Q0;
            Q0=makeQuery(id+"F15.imprint","IMPRINT",FACE,{"disambiguationData":[TD([[makeQuery(id+"F15.imprint","IMPRINT",EDGE,{"derivedFrom":sQuery(id+"F15.wireOp",EDGE,"E201")}),1.0]])]});
            var Q1;
            Q1=makeQuery(id+"F15.imprint","IMPRINT",FACE,{"disambiguationData":[TD([[makeQuery(id+"F15.imprint","IMPRINT",EDGE,{"derivedFrom":sQuery(id+"F15.wireOp",EDGE,"E204")}),1.0]])]});
            extrude(context, id + "F18", {"entities" : qUnion([Q0, Q1]), "operationType" : NewBodyOperationType.ADD, "depth" : (getVariable(context, 'mistakeLength') + getVariable(context, 'thinkress') * 3 - getVariable(context, 'nailRoundHigh') * 2) * mm, "offsetDistance" : 25 * mm});
        }
        {
            var Q0;
            Q0=makeQuery(id+"F15.imprint","IMPRINT",FACE,{"disambiguationData":[TD([[makeQuery(id+"F15.imprint","IMPRINT",EDGE,{"derivedFrom":sQuery(id+"F15.wireOp",EDGE,"E202")}),1.0]])]});
            var Q1;
            Q1=makeQuery(id+"F15.imprint","IMPRINT",FACE,{"disambiguationData":[TD([[makeQuery(id+"F15.imprint","IMPRINT",EDGE,{"derivedFrom":sQuery(id+"F15.wireOp",EDGE,"E205")}),1.0]])]});
            extrude(context, id + "F19", {"entities" : qUnion([Q0, Q1]), "operationType" : NewBodyOperationType.ADD, "depth" : (getVariable(context, 'mistakeLength') + getVariable(context, 'thinkress') * 5 - getVariable(context, 'nailRoundHigh') * 2) * mm, "offsetDistance" : 25 * mm});
        }
        {
            var Q0;
            Q0=makeQuery(id+"F15.imprint","IMPRINT",FACE,{"disambiguationData":[TD([[makeQuery(id+"F15.imprint","IMPRINT",EDGE,{"derivedFrom":sQuery(id+"F15.wireOp",EDGE,"E213")}),1.0]])]});
            var Q1;
            Q1=makeQuery(id+"F15.imprint","IMPRINT",FACE,{"disambiguationData":[TD([[makeQuery(id+"F15.imprint","IMPRINT",EDGE,{"derivedFrom":sQuery(id+"F15.wireOp",EDGE,"E218")}),1.0]])]});
            extrude(context, id + "F20", {"entities" : qUnion([Q0, Q1]), "operationType" : NewBodyOperationType.ADD, "depth" : (getVariable(context, 'mistakeLength') + 10 + getVariable(context, 'thinkress') * 2 - getVariable(context, 'nailRoundHigh') * 2) * mm, "offsetDistance" : 25 * mm});
        }
        {
            var Q0;
            Q0=makeQuery(id+"F14.opExtrude","SWEPT_EDGE",EDGE,{"disambiguationData":[OSD([sQuery(id+"F12.wireOp",EDGE,"E190"),sQuery(id+"F12.wireOp",EDGE,"E191.top"),sQuery(id+"F12.wireOp",EDGE,"E191.right")])]});
            var Q1;
            Q1=makeQuery(id+"F14.opExtrude","SWEPT_EDGE",EDGE,{"disambiguationData":[OSD([sQuery(id+"F12.wireOp",EDGE,"E190"),sQuery(id+"F12.wireOp",EDGE,"E191.bottom"),sQuery(id+"F12.wireOp",EDGE,"E191.right")])]});
            var Q2;
            Q2=makeQuery(id+"F14.opExtrude","SWEPT_EDGE",EDGE,{"disambiguationData":[OSD([sQuery(id+"F12.wireOp",EDGE,"E190"),sQuery(id+"F12.wireOp",EDGE,"E191.bottom"),sQuery(id+"F12.wireOp",EDGE,"E191.left")])]});
            var Q3;
            Q3=makeQuery(id+"F14.opExtrude","SWEPT_EDGE",EDGE,{"disambiguationData":[OSD([sQuery(id+"F12.wireOp",EDGE,"E190"),sQuery(id+"F12.wireOp",EDGE,"E191.top"),sQuery(id+"F12.wireOp",EDGE,"E191.left")])]});
            var Q4;
            Q4=makeQuery(id+"F9.boolean.opBoolean","COPY",EDGE,{"derivedFrom":makeQuery(id+"F9.opExtrude","SWEPT_EDGE",EDGE,{"disambiguationData":[OSD([sQuery(id+"F8.wireOp",EDGE,"E186"),sQuery(id+"F8.wireOp",EDGE,"E187.bottom"),sQuery(id+"F8.wireOp",EDGE,"E187.left")])]})});
            var Q5;
            Q5=makeQuery(id+"F9.boolean.opBoolean","COPY",EDGE,{"derivedFrom":makeQuery(id+"F9.opExtrude","SWEPT_EDGE",EDGE,{"disambiguationData":[OSD([sQuery(id+"F8.wireOp",EDGE,"E186"),sQuery(id+"F8.wireOp",EDGE,"E187.bottom"),sQuery(id+"F8.wireOp",EDGE,"E187.right")])]})});
            var Q6;
            Q6=makeQuery(id+"F9.boolean.opBoolean","COPY",EDGE,{"derivedFrom":makeQuery(id+"F9.opExtrude","SWEPT_EDGE",EDGE,{"disambiguationData":[OSD([sQuery(id+"F8.wireOp",EDGE,"E186"),sQuery(id+"F8.wireOp",EDGE,"E187.top"),sQuery(id+"F8.wireOp",EDGE,"E187.left")])]})});
            var Q7;
            Q7=makeQuery(id+"F9.boolean.opBoolean","COPY",EDGE,{"derivedFrom":makeQuery(id+"F9.opExtrude","SWEPT_EDGE",EDGE,{"disambiguationData":[OSD([sQuery(id+"F8.wireOp",EDGE,"E186"),sQuery(id+"F8.wireOp",EDGE,"E187.top"),sQuery(id+"F8.wireOp",EDGE,"E187.right")])]})});
            var Q8;
            Q8=makeQuery(id+"F14.opExtrude","SWEPT_EDGE",EDGE,{"disambiguationData":[OSD([sQuery(id+"F12.wireOp",EDGE,"E192"),sQuery(id+"F12.wireOp",EDGE,"E193.bottom"),sQuery(id+"F12.wireOp",EDGE,"E193.left")])]});
            var Q9;
            Q9=makeQuery(id+"F14.opExtrude","SWEPT_EDGE",EDGE,{"disambiguationData":[OSD([sQuery(id+"F12.wireOp",EDGE,"E192"),sQuery(id+"F12.wireOp",EDGE,"E193.bottom"),sQuery(id+"F12.wireOp",EDGE,"E193.right")])]});
            var Q10;
            Q10=makeQuery(id+"F14.opExtrude","SWEPT_EDGE",EDGE,{"disambiguationData":[OSD([sQuery(id+"F12.wireOp",EDGE,"E192"),sQuery(id+"F12.wireOp",EDGE,"E193.top"),sQuery(id+"F12.wireOp",EDGE,"E193.left")])]});
            var Q11;
            Q11=makeQuery(id+"F14.opExtrude","SWEPT_EDGE",EDGE,{"disambiguationData":[OSD([sQuery(id+"F12.wireOp",EDGE,"E192"),sQuery(id+"F12.wireOp",EDGE,"E193.top"),sQuery(id+"F12.wireOp",EDGE,"E193.right")])]});
            fillet(context, id + "F21", {"entities" : qUnion([Q0, Q1, Q2, Q3, Q4, Q5, Q6, Q7, Q8, Q9, Q10, Q11]), "radius" : 2.5 * mm, "allowEdgeOverflow" : false});
        }
        {
            var Q0;
            Q0=makeQuery(id+"F2.opExtrude","CAP_FACE",FACE,{"disambiguationData":[OSD([sQuery(id+"F1.wireOp",EDGE,"E35"),sQuery(id+"F1.wireOp",EDGE,"E36"),sQuery(id+"F1.wireOp",EDGE,"E37"),sQuery(id+"F1.wireOp",EDGE,"E38.0"),sQuery(id+"F1.wireOp",EDGE,"E39.0"),sQuery(id+"F1.wireOp",EDGE,"E40.0"),sQuery(id+"F1.wireOp",EDGE,"E41"),sQuery(id+"F1.wireOp",EDGE,"E42"),sQuery(id+"F1.wireOp",EDGE,"E43")])],"isStart":false});
            var sketch = newSketch(context, id + "F22", { "sketchPlane" : qUnion([Q0])});
            skLineSegment(sketch, "E220", {"start": v(1.24, -34.57) * mm, "end": v(-35.2, -69.98) * mm});
            skLineSegment(sketch, "E221", {"start": v(-35.2, -69.98) * mm, "end": v(-7.22, -62.3) * mm});
            skLineSegment(sketch, "E222", {"start": v(-7.22, -62.3) * mm, "end": v(1.24, -34.57) * mm});
            skLineSegment(sketch, "E223", {"start": v(20, -79) * mm, "end": v(13.74, -68.76) * mm});
            skLineSegment(sketch, "E224", {"start": v(13.74, -68.76) * mm, "end": v(20, -42.5) * mm});
            skLineSegment(sketch, "E225", {"start": v(20, -42.5) * mm, "end": v(20, -79) * mm});
            skLineSegment(sketch, "E226", {"start": v(-28.17, -89.03) * mm, "end": v(6.85, -91.32) * mm});
            skLineSegment(sketch, "E227", {"start": v(6.85, -91.32) * mm, "end": v(-1.84, -83.04) * mm});
            skLineSegment(sketch, "E228", {"start": v(-1.84, -83.04) * mm, "end": v(-28.17, -89.03) * mm});
            skLineSegment(sketch, "E229", {"start": v(61.24, -64.57) * mm, "end": v(24.8, -99.98) * mm});
            skLineSegment(sketch, "E230", {"start": v(24.8, -99.98) * mm, "end": v(52.78, -92.3) * mm});
            skLineSegment(sketch, "E231", {"start": v(52.78, -92.3) * mm, "end": v(61.24, -64.57) * mm});
            skLineSegment(sketch, "E232", {"start": v(80, -109) * mm, "end": v(73.74, -98.76) * mm});
            skLineSegment(sketch, "E233", {"start": v(73.74, -98.76) * mm, "end": v(80, -72.5) * mm});
            skLineSegment(sketch, "E234", {"start": v(80, -72.5) * mm, "end": v(80, -109) * mm});
            skLineSegment(sketch, "E235", {"start": v(31.83, -119.03) * mm, "end": v(66.85, -121.32) * mm});
            skLineSegment(sketch, "E236", {"start": v(66.85, -121.32) * mm, "end": v(58.16, -113.04) * mm});
            skLineSegment(sketch, "E237", {"start": v(58.16, -113.04) * mm, "end": v(31.83, -119.03) * mm});
            skSolve(sketch);
        }
        {
            var Q0;
            Q0=qSketchRegion(id+"F22",true);
            extrude(context, id + "F23", {"entities" : qUnion([Q0]), "operationType" : NewBodyOperationType.REMOVE, "endBound" : BoundingType.UP_TO_NEXT, "oppositeDirection" : true, "depth" : 25 * mm, "offsetDistance" : 25 * mm});
        }
        {
            var Q0;
            Q0=makeQuery(id+"F23.boolean.opBoolean","COPY",EDGE,{"derivedFrom":makeQuery(id+"F23.opExtrude","SWEPT_EDGE",EDGE,{"disambiguationData":[OSD([sQuery(id+"F1.wireOp",EDGE,"E39.0"),sQuery(id+"F22.wireOp",EDGE,"uJ8ptwFU-gA2U-KSwK-ShMx-xjMVscbI9hf3"),sQuery(id+"F22.wireOp",EDGE,"E224")])]})});
            var Q1;
            Q1=makeQuery(id+"F23.boolean.opBoolean","COPY",EDGE,{"derivedFrom":makeQuery(id+"F23.opExtrude","SWEPT_EDGE",EDGE,{"disambiguationData":[OSD([sQuery(id+"F22.wireOp",EDGE,"E223"),sQuery(id+"F22.wireOp",EDGE,"E224")])]})});
            var Q2;
            Q2=makeQuery(id+"F23.boolean.opBoolean","COPY",EDGE,{"derivedFrom":makeQuery(id+"F23.opExtrude","SWEPT_EDGE",EDGE,{"disambiguationData":[OSD([sQuery(id+"F1.wireOp",EDGE,"E39.0"),sQuery(id+"F22.wireOp",EDGE,"uJ8ptwFU-gA2U-KSwK-ShMx-xjMVscbI9hf3"),sQuery(id+"F22.wireOp",EDGE,"E223")])]})});
            var Q3;
            Q3=makeQuery(id+"F23.boolean.opBoolean","COPY",EDGE,{"derivedFrom":makeQuery(id+"F23.opExtrude","SWEPT_EDGE",EDGE,{"disambiguationData":[OSD([sQuery(id+"F1.wireOp",EDGE,"E40.0"),sQuery(id+"F22.wireOp",EDGE,"RIKwBn38-aO2X-G0fk-8EdH-c7k2ykc97B9S"),sQuery(id+"F22.wireOp",EDGE,"r36S6gOQ-bTYg-NTsn-zhwH-6thDepudx98D")])]})});
            var Q4;
            Q4=makeQuery(id+"F23.boolean.opBoolean","COPY",EDGE,{"derivedFrom":makeQuery(id+"F23.opExtrude","SWEPT_EDGE",EDGE,{"disambiguationData":[OSD([sQuery(id+"F22.wireOp",EDGE,"r36S6gOQ-bTYg-NTsn-zhwH-6thDepudx98D"),sQuery(id+"F22.wireOp",EDGE,"uRDFYyxu-zrTV-cAsk-tVCc-BnUGVr4wfPTn")])]})});
            var Q5;
            Q5=makeQuery(id+"F23.boolean.opBoolean","COPY",EDGE,{"derivedFrom":makeQuery(id+"F23.opExtrude","SWEPT_EDGE",EDGE,{"disambiguationData":[OSD([sQuery(id+"F1.wireOp",EDGE,"E40.0"),sQuery(id+"F22.wireOp",EDGE,"RIKwBn38-aO2X-G0fk-8EdH-c7k2ykc97B9S"),sQuery(id+"F22.wireOp",EDGE,"uRDFYyxu-zrTV-cAsk-tVCc-BnUGVr4wfPTn")])]})});
            var Q6;
            Q6=makeQuery(id+"F23.boolean.opBoolean","COPY",EDGE,{"derivedFrom":makeQuery(id+"F23.opExtrude","SWEPT_EDGE",EDGE,{"disambiguationData":[OSD([sQuery(id+"F1.wireOp",EDGE,"E38.0"),sQuery(id+"F22.wireOp",EDGE,"E220"),sQuery(id+"F22.wireOp",EDGE,"E221")])]})});
            var Q7;
            Q7=makeQuery(id+"F23.boolean.opBoolean","COPY",EDGE,{"derivedFrom":makeQuery(id+"F23.opExtrude","SWEPT_EDGE",EDGE,{"disambiguationData":[OSD([sQuery(id+"F22.wireOp",EDGE,"E221"),sQuery(id+"F22.wireOp",EDGE,"E222")])]})});
            var Q8;
            Q8=makeQuery(id+"F23.boolean.opBoolean","COPY",EDGE,{"derivedFrom":makeQuery(id+"F23.opExtrude","SWEPT_EDGE",EDGE,{"disambiguationData":[OSD([sQuery(id+"F1.wireOp",EDGE,"E38.0"),sQuery(id+"F22.wireOp",EDGE,"E220"),sQuery(id+"F22.wireOp",EDGE,"E222")])]})});
            var Q9;
            Q9=makeQuery(id+"F23.boolean.opBoolean","COPY",EDGE,{"derivedFrom":makeQuery(id+"F23.opExtrude","SWEPT_EDGE",EDGE,{"disambiguationData":[OSD([sQuery(id+"F22.wireOp",EDGE,"E227"),sQuery(id+"F22.wireOp",EDGE,"E228")])]})});
            var Q10;
            Q10=makeQuery(id+"F23.boolean.opBoolean","COPY",EDGE,{"derivedFrom":makeQuery(id+"F23.opExtrude","SWEPT_EDGE",EDGE,{"disambiguationData":[OSD([sQuery(id+"F22.wireOp",EDGE,"E235"),sQuery(id+"F22.wireOp",EDGE,"E237")])]})});
            var Q11;
            Q11=makeQuery(id+"F23.boolean.opBoolean","COPY",EDGE,{"derivedFrom":makeQuery(id+"F23.opExtrude","SWEPT_EDGE",EDGE,{"disambiguationData":[OSD([sQuery(id+"F22.wireOp",EDGE,"E236"),sQuery(id+"F22.wireOp",EDGE,"E237")])]})});
            var Q12;
            Q12=makeQuery(id+"F23.boolean.opBoolean","COPY",EDGE,{"derivedFrom":makeQuery(id+"F23.opExtrude","SWEPT_EDGE",EDGE,{"disambiguationData":[OSD([sQuery(id+"F22.wireOp",EDGE,"E235"),sQuery(id+"F22.wireOp",EDGE,"E236")])]})});
            var Q13;
            Q13=makeQuery(id+"F23.boolean.opBoolean","COPY",EDGE,{"derivedFrom":makeQuery(id+"F23.opExtrude","SWEPT_EDGE",EDGE,{"disambiguationData":[OSD([sQuery(id+"F22.wireOp",EDGE,"E232"),sQuery(id+"F22.wireOp",EDGE,"E233")])]})});
            var Q14;
            Q14=makeQuery(id+"F23.boolean.opBoolean","COPY",EDGE,{"derivedFrom":makeQuery(id+"F23.opExtrude","SWEPT_EDGE",EDGE,{"disambiguationData":[OSD([sQuery(id+"F22.wireOp",EDGE,"E232"),sQuery(id+"F22.wireOp",EDGE,"E234")])]})});
            var Q15;
            Q15=makeQuery(id+"F23.boolean.opBoolean","COPY",EDGE,{"derivedFrom":makeQuery(id+"F23.opExtrude","SWEPT_EDGE",EDGE,{"disambiguationData":[OSD([sQuery(id+"F22.wireOp",EDGE,"E233"),sQuery(id+"F22.wireOp",EDGE,"E234")])]})});
            var Q16;
            Q16=makeQuery(id+"F23.boolean.opBoolean","COPY",EDGE,{"derivedFrom":makeQuery(id+"F23.opExtrude","SWEPT_EDGE",EDGE,{"disambiguationData":[OSD([sQuery(id+"F22.wireOp",EDGE,"E230"),sQuery(id+"F22.wireOp",EDGE,"E231")])]})});
            var Q17;
            Q17=makeQuery(id+"F23.boolean.opBoolean","COPY",EDGE,{"derivedFrom":makeQuery(id+"F23.opExtrude","SWEPT_EDGE",EDGE,{"disambiguationData":[OSD([sQuery(id+"F22.wireOp",EDGE,"E229"),sQuery(id+"F22.wireOp",EDGE,"E231")])]})});
            var Q18;
            Q18=makeQuery(id+"F23.boolean.opBoolean","COPY",EDGE,{"derivedFrom":makeQuery(id+"F23.opExtrude","SWEPT_EDGE",EDGE,{"disambiguationData":[OSD([sQuery(id+"F22.wireOp",EDGE,"E229"),sQuery(id+"F22.wireOp",EDGE,"E230")])]})});
            fillet(context, id + "F24", {"entities" : qUnion([Q0, Q1, Q2, Q3, Q4, Q5, Q6, Q7, Q8, Q9, Q10, Q11, Q12, Q13, Q14, Q15, Q16, Q17, Q18]), "radius" : 10 * mm, "allowEdgeOverflow" : false});
        }
        {
            var Q0;
            Q0=makeQuery(id+"F2.opExtrude","CAP_FACE",FACE,{"disambiguationData":[OSD([sQuery(id+"F1.wireOp",EDGE,"E55"),sQuery(id+"F1.wireOp",EDGE,"E56"),sQuery(id+"F1.wireOp",EDGE,"E57"),sQuery(id+"F1.wireOp",EDGE,"E58"),sQuery(id+"F1.wireOp",EDGE,"E59"),sQuery(id+"F1.wireOp",EDGE,"E60"),sQuery(id+"F1.wireOp",EDGE,"E61"),sQuery(id+"F1.wireOp",EDGE,"E62"),sQuery(id+"F1.wireOp",EDGE,"E63"),sQuery(id+"F1.wireOp",EDGE,"E64"),sQuery(id+"F1.wireOp",EDGE,"E65"),sQuery(id+"F1.wireOp",EDGE,"E92"),sQuery(id+"F1.wireOp",EDGE,"E93"),sQuery(id+"F1.wireOp",EDGE,"E94.bottom"),sQuery(id+"F1.wireOp",EDGE,"E94.top"),sQuery(id+"F1.wireOp",EDGE,"E95"),sQuery(id+"F1.wireOp",EDGE,"E97.filletArc"),sQuery(id+"F1.wireOp",EDGE,"E98.filletArc"),sQuery(id+"F1.wireOp",EDGE,"E99.filletArc"),sQuery(id+"F1.wireOp",EDGE,"E100.filletArc"),sQuery(id+"F1.wireOp",EDGE,"E101.trimOffspring")])],"isStart":true});
            var sketch = newSketch(context, id + "F25", { "sketchPlane" : qUnion([Q0])});
            skCircle(sketch, "E238", {"center": v(-105.49, -18.11) * mm, "radius": 1.5 * mm});
            skCircle(sketch, "E239.0", {"center": v(-105.49, -18.11) * mm, "radius": 3.25 * mm});
            skSolve(sketch);
        }
        {
            var Q0;
            Q0=makeQuery(id+"F25.imprint","IMPRINT",FACE,{"disambiguationData":[TD([[makeQuery(id+"F25.imprint","IMPRINT",EDGE,{"derivedFrom":sQuery(id+"F25.wireOp",EDGE,"E238")}),-1.0]])]});
            extrude(context, id + "F26", {"entities" : qUnion([Q0]), "operationType" : NewBodyOperationType.ADD, "oppositeDirection" : true, "depth" : 1 * mm, "offsetDistance" : 25 * mm});
        }
        {
            var Q0;
            Q0=makeQuery(id+"F2.opExtrude","SWEPT_BODY",BODY,{"disambiguationData":[OSD([sQuery(id+"F1.wireOp",EDGE,"E55"),sQuery(id+"F1.wireOp",EDGE,"E56"),sQuery(id+"F1.wireOp",EDGE,"E57"),sQuery(id+"F1.wireOp",EDGE,"E58"),sQuery(id+"F1.wireOp",EDGE,"E59"),sQuery(id+"F1.wireOp",EDGE,"E60"),sQuery(id+"F1.wireOp",EDGE,"E61"),sQuery(id+"F1.wireOp",EDGE,"E62"),sQuery(id+"F1.wireOp",EDGE,"E63"),sQuery(id+"F1.wireOp",EDGE,"E64"),sQuery(id+"F1.wireOp",EDGE,"E65"),sQuery(id+"F1.wireOp",EDGE,"E92"),sQuery(id+"F1.wireOp",EDGE,"E93"),sQuery(id+"F1.wireOp",EDGE,"E94.bottom"),sQuery(id+"F1.wireOp",EDGE,"E94.top"),sQuery(id+"F1.wireOp",EDGE,"E95"),sQuery(id+"F1.wireOp",EDGE,"E97.filletArc"),sQuery(id+"F1.wireOp",EDGE,"E98.filletArc"),sQuery(id+"F1.wireOp",EDGE,"E99.filletArc"),sQuery(id+"F1.wireOp",EDGE,"E100.filletArc"),sQuery(id+"F1.wireOp",EDGE,"E101.trimOffspring")])]});
            transform(context, id + "F27", {"entities" : qUnion([Q0]), "transformType" : TransformType.TRANSLATION_3D, "dx" : 0 * mm, "dy" : 0 * mm, "dz" : 0 * mm, "makeCopy" : true});
        }
    });
